# Revit family: QF_ELECTROLUXPROFESSIONAL_586839_PUEN17ELEM
name_source: partatom
category: Specialty Equipment
revit_build: Autodesk Revit 2018 (Build: 20190510_1515(x64)
units: mm (PartAtom-declared; Revit-internal decimal feet)

## family parameters
Always vertical = Yes
Cut with Voids When Loaded = No
Part Type = Normal
Room Calculation Point = No
Round Connector Dimension = Use Radius
Shared = Yes
Work Plane-Based = No

## types (1)
- 586839_EL. STAT.PRESS. BRAIS. PAN+STEAM_TAP._170LT (H)_C
    50 Hertz Option = No
    60 Hertz Option = Yes
    Apparent Power = 0 VA
    Base Height = 200 mm  [stored 0.656168 ft]
    Code = 0
    Cold Water Connection Height = 635 mm
    Cold Water Size = 1"
    Conn Conduit = Yes
    Cycle = 60 Hz
    Depth = 900 mm  [stored 2.95276 ft]
    Description = High Productivity Cooking Electric Pressure Braising Pan-170lt Hygienic Profile-Backsplash with Tap
    Direct Waste Size = 0"
    Electrical Remarks = 3PH+N 50/60HZ COMPATIBLE
    FL Amps = 0 A
    HP = 27.6 HP
    Height = 900 mm  [stored 2.95276 ft]
    Hot Water Connection Height = 715 mm
    Hot Water Size = 1"
    Indirect Waste Connection Height = 0 mm  [stored 0 ft]
    Indirect Waste Radius Size = 25.4 mm  [stored 0.0833333 ft]
    Indirect Waste Size = 2"
    Manufacturer = ELECTROLUX
    Max Overcurrent Protection = 5 A
    Min Ckt Ampacity = 0 A
    Model = 586839
    Phase = 3
    URL = www.electrolux.com/foodservice
    URL Cutsheet = www.electrolux.com/foodservice
    URL Manufacturer = www.electrolux.com/foodservice
    Volts = 400 V
    Watts = 0 W
    Weight = 310 kg
    Width = 1400 mm  [stored 4.59318 ft]

note: [stored X ft] marks values corroborated as IEEE doubles in the binary element streams (Revit-internal decimal feet)

## geometry (parser evidence)
native form markers: Blend x14, Sweep x5
no freeform markers — native parametric forms only
